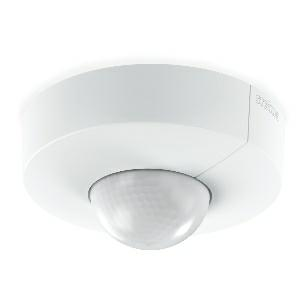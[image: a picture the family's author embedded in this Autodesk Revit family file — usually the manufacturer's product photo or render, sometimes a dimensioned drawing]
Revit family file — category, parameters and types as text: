
# Revit family: is_345_057299
name_source: partatom
category: Elektroinstallationen
revit_build: Autodesk Revit 2016 (Build: 20190508_0715(x64)
units: mm (PartAtom-declared; Revit-internal decimal feet)

## family parameters
Basisbauteil = Fläche
Beim Laden mit Abzugskörper schneiden = Nein
Bemaßung runder Anschluss = Durchmesser verwenden
Beschriftungsausrichtung beibehalten = Nein
Gemeinsam genutzt = Nein
Raumberechnungspunkt = Nein
Teiletyp = Normal

## types (1)
- IS 345
    Apparent Load = 0 VA
    Beschreibung = Type: Motion detectors; Dimensions (Ø x H): 126 x 78 mm; Mains power supply: 12 – 22,5 V / 50 – 60 Hz; Sensor Technology: passive infrared; Application, place: Outdoors, Indoors; Application, room: corridor / aisle, multi-storey / underground car park, outdoors, Indoors; Installation site: ceiling; Installation: Surface wiring; Switching zones: 280 switching zones; Electronic scalability: No; Mechanical scalability: No; Mounting height: 2,5 – 5 m; Optimum mounting height: 2,8 m; Detection angle: 360 °; Angle of aperture: 45 °; Sneak-by guard: Yes; Capability of masking out individual segments: Yes; Reach, radial: 12 x 6 m (72 m²); Reach, tangential: 23 x 6 m (138 m²); Twilight setting TEACH: Yes; Twilight setting: 2 – 1000 lx; Time setting: 5 sec – 15 min; Control output, Dali: Addressable/slave; Constant-lighting control: No; Basic light level function: No; Basic light level function time: 1-30 min, all night; With bus coupling: Yes; Settings via: Bus; With remote control: No; Interconnection: Yes; IP-rating: IP54; Material: Plastic; Ambient temperature: -20 – 50 °C; Colour: white; Colour, RAL: 9003; Manufacturer's Warranty: 5 years; Version: DALI-2 IPD - surface, rd.; PU1, EAN: 4007841057299
    Height = 0 mm  [stored 0 ft]
    Hersteller = Steinel
    Length = 126 mm
    Maximum range = 11.589 m
    ModVariant = Nein
    Modell = 057299
    Mounting Place = Ceiling
    Mounting Type = Surface mounted
    Number of Poles = 1
    OnlyDefault = Ja
    Power Factor = 1
    Product Name = IS 345
    Product group = Sensor-switched outdoor light
    ProductGroupID = 3
    Protection Class = Protection class
    Protection Degree = IP 54
    RlxData = <blob elided: 156349 chars, md5=2bedfa67>
    Sensor characteristics = Stretched
    Sensor type = Passive (infrared)
    SensorDataFile = <blob elided: 5885 chars, md5=98bccc25>
    Type of entry = Motion
    Typenbild = produkt1_057299.jpg
    Typenkommentare = Product without accessories
    URL = http://relux.com
    VarID = ---
    Voltage = 0 V
    Vorgabe-Ansicht = 1800 mm
    Weight = 0.00 kg
    Width = 0 mm  [stored 0 ft]

note: [stored X ft] marks values corroborated as IEEE doubles in the binary element streams (Revit-internal decimal feet)

## geometry (parser evidence)
native form markers: Blend x4, Sweep x19
no freeform markers — native parametric forms only
